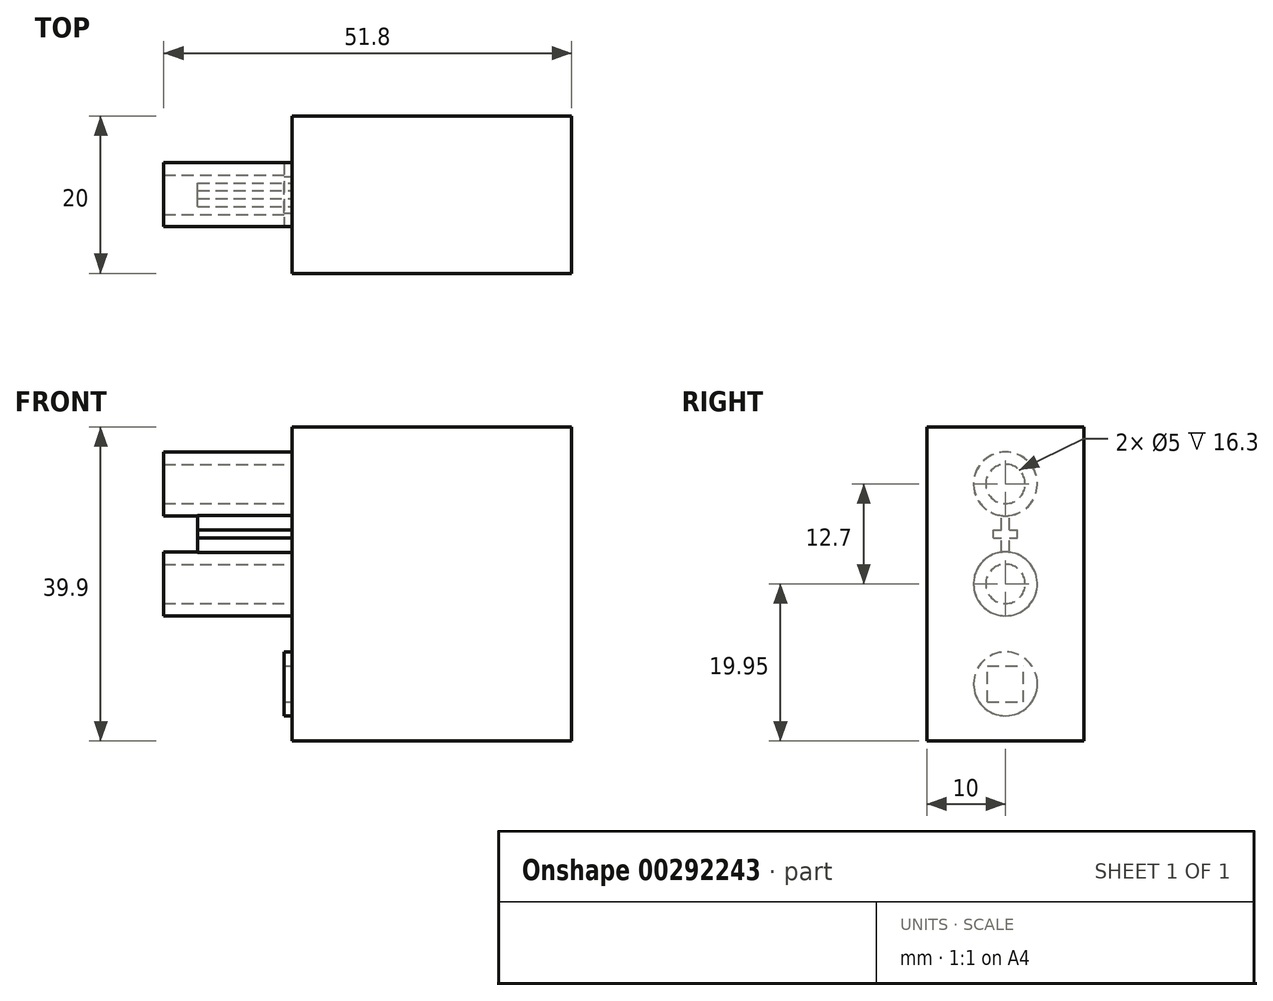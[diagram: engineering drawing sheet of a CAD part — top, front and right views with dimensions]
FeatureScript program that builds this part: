
annotation { "Feature Type Name" : "Feature", "Feature Type Description" : "" }
export const myFeature = defineFeature(function(context is Context, id is Id, definition is map)
    precondition{}
    {
        {
            var Q0;
            Q0=qCreatedBy(makeId("Top.planeOp"),FACE);
            var sketch = newSketch(context, id + "F0", { "sketchPlane" : qUnion([Q0])});
            skLineSegment(sketch, "E0.bottom", {"start": v(17.75, 19.95) * mm, "end": v(-17.75, 19.95) * mm});
            skLineSegment(sketch, "E0.top", {"start": v(17.75, -19.95) * mm, "end": v(-17.75, -19.95) * mm});
            skLineSegment(sketch, "E0.left", {"start": v(17.75, 19.95) * mm, "end": v(17.75, -19.95) * mm});
            skLineSegment(sketch, "E0.right", {"start": v(-17.75, 19.95) * mm, "end": v(-17.75, -19.95) * mm});
            skPoint(sketch, "E0.middle", {"position": v(0, 0) * mm});
            skSolve(sketch);
        }
        {
            var Q0;
            Q0=makeQuery(id+"F0.imprint","IMPRINT",FACE,{"disambiguationData":[TD([[makeQuery(id+"F0.imprint","IMPRINT",EDGE,{"derivedFrom":sQuery(id+"F0.wireOp",EDGE,"E0.bottom")}),1.0]])]});
            extrude(context, id + "F1", {"entities" : qUnion([Q0]), "depth" : 20 * mm});
        }
        {
            var Q0;
            Q0=makeQuery(id+"F1.opExtrude","SWEPT_FACE",FACE,{"disambiguationData":[OSD([sQuery(id+"F0.wireOp",EDGE,"E0.right")])]});
            var sketch = newSketch(context, id + "F2", { "sketchPlane" : qUnion([Q0])});
            skLineSegment(sketch, "E1", {"start": v(19.95, 10) * mm, "end": v(0, 10) * mm});
            skLineSegment(sketch, "E2", {"start": v(0, 10) * mm, "end": v(12.7, 10) * mm});
            skLineSegment(sketch, "E3", {"start": v(12.7, 10) * mm, "end": v(-2.5, 10) * mm});
            skCircle(sketch, "E4", {"center": v(0, 10) * mm, "radius": 4.05 * mm});
            skCircle(sketch, "E5", {"center": v(-12.7, 10) * mm, "radius": 4.05 * mm});
            skCircle(sketch, "E6", {"center": v(12.7, 10) * mm, "radius": 4.05 * mm});
            skLineSegment(sketch, "E7.bottom", {"start": v(15, 12.3) * mm, "end": v(10.39, 12.3) * mm});
            skLineSegment(sketch, "E7.top", {"start": v(15, 7.69) * mm, "end": v(10.39, 7.69) * mm});
            skLineSegment(sketch, "E7.left", {"start": v(15, 12.3) * mm, "end": v(15, 7.69) * mm});
            skLineSegment(sketch, "E7.right", {"start": v(10.39, 12.3) * mm, "end": v(10.39, 7.69) * mm});
            skCircle(sketch, "E8", {"center": v(-12.7, 10) * mm, "radius": 2.5 * mm});
            skCircle(sketch, "E9", {"center": v(0, 10) * mm, "radius": 2.5 * mm});
            skPoint(sketch, "E10.orphan", {"position": v(-19.95, 10) * mm});
            skLineSegment(sketch, "E11.trimOffspring", {"start": v(-2.5, 10) * mm, "end": v(19.95, 10) * mm});
            skLineSegment(sketch, "E12.bottom", {"start": v(-4.02, 10.5) * mm, "end": v(-5.85, 10.5) * mm});
            skLineSegment(sketch, "E12.top", {"start": v(-4.02, 9.5) * mm, "end": v(-5.85, 9.5) * mm});
            skPoint(sketch, "E12.middle", {"position": v(-6.35, 10) * mm});
            skLineSegment(sketch, "E13.bottom", {"start": v(-5.85, 11.5) * mm, "end": v(-6.85, 11.5) * mm});
            skLineSegment(sketch, "E13.top", {"start": v(-5.85, 8.5) * mm, "end": v(-6.85, 8.5) * mm});
            skLineSegment(sketch, "E13.left", {"start": v(-5.85, 11.5) * mm, "end": v(-5.85, 10.5) * mm});
            skLineSegment(sketch, "E13.right", {"start": v(-6.85, 11.5) * mm, "end": v(-6.85, 10.5) * mm});
            skLineSegment(sketch, "E14.trimOffspring", {"start": v(-6.85, 9.5) * mm, "end": v(-6.85, 8.5) * mm});
            skLineSegment(sketch, "E15.trimOffspring", {"start": v(-6.85, 9.5) * mm, "end": v(-8.68, 9.5) * mm});
            skLineSegment(sketch, "E16.trimOffspring", {"start": v(-6.85, 10.5) * mm, "end": v(-8.68, 10.5) * mm});
            skLineSegment(sketch, "E17.trimOffspring", {"start": v(-5.85, 9.5) * mm, "end": v(-5.85, 8.5) * mm});
            skPoint(sketch, "E18.trimOffspring.end.orphan", {"position": v(-4.05, 10) * mm});
            skPoint(sketch, "E19.orphan", {"position": v(-8.84, 10.5) * mm});
            skPoint(sketch, "E20.orphan", {"position": v(-8.84, 9.5) * mm});
            skPoint(sketch, "E12.left.end.orphan", {"position": v(-3.86, 9.5) * mm});
            skPoint(sketch, "E12.left.start.orphan", {"position": v(-3.86, 10.5) * mm});
            skPoint(sketch, "E21.trimOffspring.start.orphan", {"position": v(-8.65, 10) * mm});
            skSolve(sketch);
        }
        {
            var Q0;
            Q0=makeQuery(id+"F2.imprint","IMPRINT",FACE,{"disambiguationData":[TD([[makeQuery(id+"F2.imprint","IMPRINT",EDGE,{"derivedFrom":sQuery(id+"F2.wireOp",EDGE,"E8")}),-1.0]])]});
            var Q1;
            {var subQ4=sQuery(id+"F2.wireOp",EDGE,"E4");var subQ6=makeQuery(id+"F2.imprint","IMPRINT",VERTEX,{"derivedFrom":subQ4});Q1=makeQuery(id+"F2.imprint","IMPRINT",FACE,{"disambiguationData":[TD([[makeQuery(id+"F2.imprint","IMPRINT",EDGE,{"disambiguationData":[TD([[subQ6,-1.0]])],"derivedFrom":subQ4}),1.0]])]});}
            extrude(context, id + "F3", {"entities" : qUnion([Q0, Q1]), "operationType" : NewBodyOperationType.ADD, "depth" : 16.3 * mm});
        }
        {
            var Q0;
            {var subQ3=sQuery(id+"F2.wireOp",EDGE,"E12.bottom");Q0=makeQuery(id+"F2.imprint","IMPRINT",FACE,{"disambiguationData":[TD([[makeQuery(id+"F2.imprint","IMPRINT",EDGE,{"derivedFrom":subQ3}),1.0]])]});}
            extrude(context, id + "F4", {"entities" : qUnion([Q0]), "operationType" : NewBodyOperationType.ADD, "depth" : 12 * mm});
        }
        {
            var Q0;
            {var subQ1=sQuery(id+"F2.wireOp",EDGE,"E7.bottom");Q0=makeQuery(id+"F2.imprint","IMPRINT",FACE,{"disambiguationData":[TD([[makeQuery(id+"F2.imprint","IMPRINT",EDGE,{"derivedFrom":subQ1}),-1.0]])]});}
            var Q1;
            {var subQ1=sQuery(id+"F2.wireOp",EDGE,"E7.top");Q1=makeQuery(id+"F2.imprint","IMPRINT",FACE,{"disambiguationData":[TD([[makeQuery(id+"F2.imprint","IMPRINT",EDGE,{"derivedFrom":subQ1}),1.0]])]});}
            extrude(context, id + "F5", {"entities" : qUnion([Q0, Q1]), "operationType" : NewBodyOperationType.ADD, "depth" : 1 * mm});
        }
        {
            var Q0;
            Q0=makeQuery(id+"F1.opExtrude","SWEPT_BODY",BODY,{"disambiguationData":[OSD([sQuery(id+"F0.wireOp",EDGE,"E0.bottom"),sQuery(id+"F0.wireOp",EDGE,"E0.top"),sQuery(id+"F0.wireOp",EDGE,"E0.left"),sQuery(id+"F0.wireOp",EDGE,"E0.right")])]});
            var Q1;
            Q1=makeQuery(id+"F1.opExtrude","CAP_EDGE",EDGE,{"disambiguationData":[OSD([sQuery(id+"F0.wireOp",EDGE,"E0.top")])],"isStart":false});
            transform(context, id + "F6", {"entities" : qUnion([Q0]), "transformType" : TransformType.ROTATION, "transformAxis" : qUnion([Q1]), "angle" : 90 * degree, "oppositeDirection" : true, "makeCopy" : false});
        }
    });
